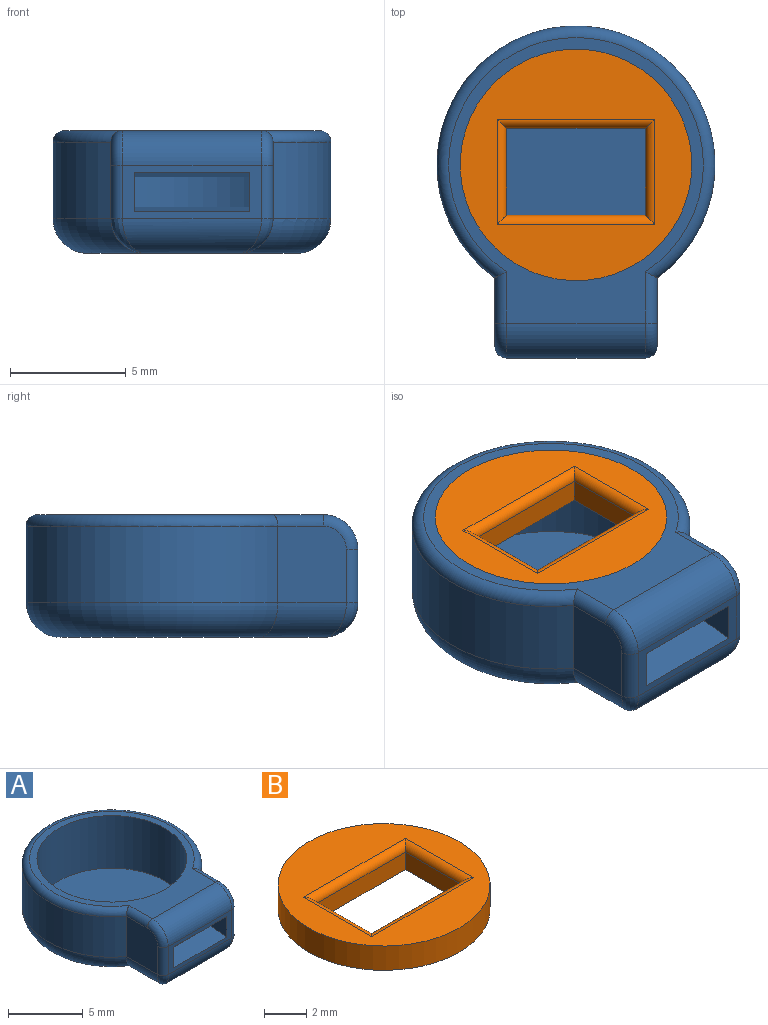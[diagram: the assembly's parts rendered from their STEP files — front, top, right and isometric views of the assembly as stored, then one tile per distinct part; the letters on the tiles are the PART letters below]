
ASSEMBLY  parts=2 mates=1
PART A: 28 faces, bbox 13x14.9x5.4 mm
  f0: plane 4x1.7mm, normal (-1,0,0), area 5.5mm2, adj f6,f8,f14,f15,f26,f27
  f1: plane 4x1.7mm, normal (1,0,0), area 5.5mm2, adj f6,f8,f14,f15,f26,f27
  f2: plane 12.33x11mm, normal (0,0,1), area 26.2mm2, adj f8,f16,f20,f21,f22
  f3: plane 3.3x2.96mm, normal (1,0,0), area 9.5mm2, adj f4,f12,f22,f23,f24
  f4: cylinder r=6mm len=12mm, axis (0,0,1), area 99.7mm2, adj f3,f5,f10,f21
  f5: plane 3.3x2.96mm, normal (-1,0,0), area 9.5mm2, adj f4,f11,f18,f19,f20
  f6: plane 6x2.3mm, normal (0,-1,0), area 5.3mm2, adj f0,f1,f13,f16,f18,f24,f26,f27
  f7: plane 11.33x9mm, normal (0,0,-1), area 73.5mm2, adj f10,f11,f12,f13
  f8: cylinder r=5mm len=10mm, axis (0,0,1), area 128.3mm2, adj f0,f1,f2,f9,f14,f15
  f9: plane 10x10mm, normal (0,0,1), area 78.5mm2, adj f8
  f10: torus R=4.5mm, axis (0,0,1), area 66mm2, adj f4,f7,f11,f12
  f11: cylinder r=1.5mm len=3.8mm, axis (0,1,0), area 6.8mm2, adj f5,f7,f10,f17
  f12: cylinder r=1.5mm len=3.8mm, axis (0,-1,0), area 6.8mm2, adj f3,f7,f10,f25
  f13: cylinder r=1.5mm len=6mm, axis (-1,0,0), area 12.4mm2, adj f6,f7,f17,f25
  f14: plane 5x2.5mm, normal (0,0,1), area 10.2mm2, adj f0,f1,f8,f26
  f15: plane 5x2.5mm, normal (0,0,-1), area 10.2mm2, adj f0,f1,f8,f27
  f16: cylinder r=1.5mm len=6mm, axis (1,0,0), area 14.1mm2, adj f2,f6,f19,f23
  f17: bspline ~1.76x1.5mm, area 1.3mm2, adj f11,f13,f18
  f18: cylinder r=0.5mm len=2.3mm, axis (0,0,1), area 1.8mm2, adj f5,f6,f17,f19
  f19: torus R=1mm, axis (-1,0,0), area 1.6mm2, adj f5,f16,f18,f20
  f20: cylinder r=0.5mm len=2.22mm, axis (0,-1,0), area 1.6mm2, adj f2,f5,f19,f21
  f21: torus R=5.5mm, axis (0,0,1), area 23.2mm2, adj f2,f4,f20,f22
  f22: cylinder r=0.5mm len=2.22mm, axis (0,1,0), area 1.6mm2, adj f2,f3,f21,f23
  f23: torus R=1mm, axis (-1,0,0), area 1.6mm2, adj f3,f16,f22,f24
  f24: cylinder r=0.5mm len=2.3mm, axis (0,0,-1), area 1.8mm2, adj f3,f6,f23,f25
  f25: bspline ~1.57x1.5mm, area 1.3mm2, adj f12,f13,f24
  f26: plane 5x1.5mm, normal (0,-0.13,0.99), area 7.6mm2, adj f0,f1,f6,f14
  f27: plane 5x1.5mm, normal (0,-0.13,-0.99), area 7.6mm2, adj f0,f1,f6,f15
PART B: 11 faces, bbox 10x10x1.4 mm
  f0: plane 3.75x1mm, normal (1,0,0), area 3.8mm2, adj f1,f4,f5,f7
  f1: plane 6x1mm, normal (0,-1,0), area 6mm2, adj f0,f2,f5,f8
  f2: plane 3.75x1mm, normal (-1,0,0), area 3.8mm2, adj f1,f4,f5,f10
  f3: cylinder r=5mm len=10mm, axis (0,0,1), area 44mm2, adj f5,f6
  f4: plane 6x1mm, normal (0,1,0), area 6mm2, adj f0,f2,f5,f9
  f5: plane 10x10mm, normal (0,0,-1), area 56mm2, adj f0,f1,f2,f3,f4
  f6: plane 10x10mm, normal (0,0,1), area 47.6mm2, adj f3,f7,f8,f9,f10
  f7: cylinder r=0.4mm len=4.55mm, axis (0,1,0), area 2.5mm2, adj f0,f6,f8,f9
  f8: cylinder r=0.4mm len=6.8mm, axis (1,0,0), area 4mm2, adj f1,f6,f7,f10
  f9: cylinder r=0.4mm len=6.8mm, axis (-1,0,0), area 4mm2, adj f4,f6,f7,f10
  f10: cylinder r=0.4mm len=4.55mm, axis (0,-1,0), area 2.5mm2, adj f2,f6,f8,f9
PLACE A t=(18.01,-1.36,0.15)mm
PLACE B t=(18.01,-1.36,0.15)mm
MATE slider B.f3 <-> A.f4  axis (0,0,1) through (18.01,-1.36,0.15)mm
